# Revit family: КО РАШВОРК  арт.404
name_source: partatom
category: Арматура трубопроводов
units: mm (PartAtom-declared; Revit-internal decimal feet)

## family parameters
Всегда вертикально = Нет
На основе рабочей плоскости = Нет
Общий = Нет
При загрузке вырезать с полостями = Нет
Размер круглого соединителя = Использовать диаметр
Тип детали = Клапан - Вставляется

## types (12) — shared parameters
ADSK_Единица измерения = шт
ADSK_Завод-изготовитель = ООО ТД "РАШВОРК"
HHH = 2 мм
URL = https://rwru.ru
Изготовитель = ООО ТД "РАШВОРК"
Материал корпус = нерж.сталь CF8M
Материал тарелка = нерж.сталь CF8M
zero-valued in all types: Отметка по умолчанию

## per-type parameters (varying)
| type | ADSK_Код изделия | ADSK_Масса | D1_2 | D2_2 | DDD | DN_2 | DNсоед. | D_2 | H | Hфаск | L | L1 | Lфаск | h |
| Клапан обратный тарельчатый РАШВОРК 404-015-40, DN015 PN40, корпус - CF8M, диск - CF8M, уплотнение - CF8M, М/Ф | 404-015-40 | 0.09 | 14 мм | 16 мм | 13 мм | 8 мм | 15 мм | 20 мм | 4 мм | 16 мм | 16 мм | 6 мм | 8 мм | 2 мм |
| Клапан обратный тарельчатый РАШВОРК 404-200-40, DN200 PN40, корпус - CF8M, диск - CF8M, уплотнение - CF8M, М/Ф | 404-200-40 | 16.1 | 120 мм | 131 мм | 119 мм | 93 мм | 200 мм | 137 мм | 32 мм | 134 мм | 140 мм | 6 мм | 18 мм | 2 мм |
| Клапан обратный тарельчатый РАШВОРК 404-020-40, DN020 PN40, корпус - CF8M, диск - CF8M, уплотнение - CF8M, М/Ф | 404-020-40 | 0.12 | 18 мм | 20 мм | 17 мм | 10 мм | 20 мм | 23 мм | 3 мм | 21 мм | 19 мм | 6 мм | 8 мм | 2 мм |
| Клапан обратный тарельчатый РАШВОРК 404-025-40, DN025 PN40, корпус - CF8M, диск - CF8M, уплотнение - CF8M, М/Ф | 404-025-40 | 0.16 | 22 мм | 23 мм | 20 мм | 13 мм | 25 мм | 27 мм | 3 мм | 24 мм | 21 мм | 7 мм | 8 мм | 2 мм |
| Клапан обратный тарельчатый РАШВОРК 404-032-40, DN032 PN40, корпус - CF8M, диск - CF8M, уплотнение - CF8M, М/Ф | 404-032-40 | 0.31 | 28 мм | 30 мм | 25 мм | 16 мм | 32 мм | 35 мм | 3 мм | 32 мм | 27 мм | 7 мм | 8 мм | 4 мм |
| Клапан обратный тарельчатый РАШВОРК 404-040-40, DN040 PN40, корпус - CF8M, диск - CF8M, уплотнение - CF8M, М/Ф | 404-040-40 | 0.43 | 34 мм | 36 мм | 33 мм | 20 мм | 40 мм | 42 мм | 4 мм | 38 мм | 31 мм | 7 мм | 8 мм | 6 мм |
| Клапан обратный тарельчатый РАШВОРК 404-050-40, DN050 PN40, корпус - CF8M, диск - CF8M, уплотнение - CF8M, М/Ф | 404-050-40 | 0.78 | 40 мм | 42 мм | 39 мм | 25 мм | 50 мм | 48 мм | 4 мм | 44 мм | 40 мм | 8 мм | 8 мм | 8 мм |
| Клапан обратный тарельчатый РАШВОРК 404-065-40, DN065 PN40, корпус - CF8M, диск - CF8M, уплотнение - CF8M, М/Ф | 404-065-40 | 1.03 | 50 мм | 52 мм | 46 мм | 31 мм | 65 мм | 58 мм | 6 мм | 53 мм | 46 мм | 8 мм | 8 мм | 8 мм |
| Клапан обратный тарельчатый РАШВОРК 404-080-40, DN080 PN40, корпус - CF8M, диск - CF8M, уплотнение - CF8M, М/Ф | 404-080-40 | 1.54 | 59 мм | 62 мм | 57 мм | 31 мм | 80 мм | 68 мм | 6 мм | 63 мм | 50 мм | 10 мм | 10 мм | 11 мм |
| Клапан обратный тарельчатый РАШВОРК 404-100-40, DN100 PN40, корпус - CF8M, диск - CF8M, уплотнение - CF8M, М/Ф | 404-100-40 | 2.25 | 68 мм | 70 мм | 66 мм | 31 мм | 100 мм | 77 мм | 7 мм | 73 мм | 60 мм | 10 мм | 10 мм | 16 мм |
| Клапан обратный тарельчатый РАШВОРК 404-125-40, DN125 PN40, корпус - CF8M, диск - CF8M, уплотнение - CF8M, М/Ф | 404-125-40 | 5.5 | 80 мм | 89 мм | 74 мм | 59 мм | 125 мм | 94 мм | 12 мм | 91 мм | 90 мм | 12 мм | 15 мм | 16 мм |
| Клапан обратный тарельчатый РАШВОРК 404-150-40, DN150 PN40, корпус - CF8M, диск - CF8M, уплотнение - CF8M, М/Ф | 404-150-40 | 8.3 | 94 мм | 103 мм | 92 мм | 70 мм | 150 мм | 109 мм | 12 мм | 106 мм | 106 мм | 12 мм | 15 мм | 15 мм |

note: column(s) folded — value = type name in every type: ADSK_Наименование

## geometry (parser evidence)
native form markers: Blend x4
no freeform markers — native parametric forms only
